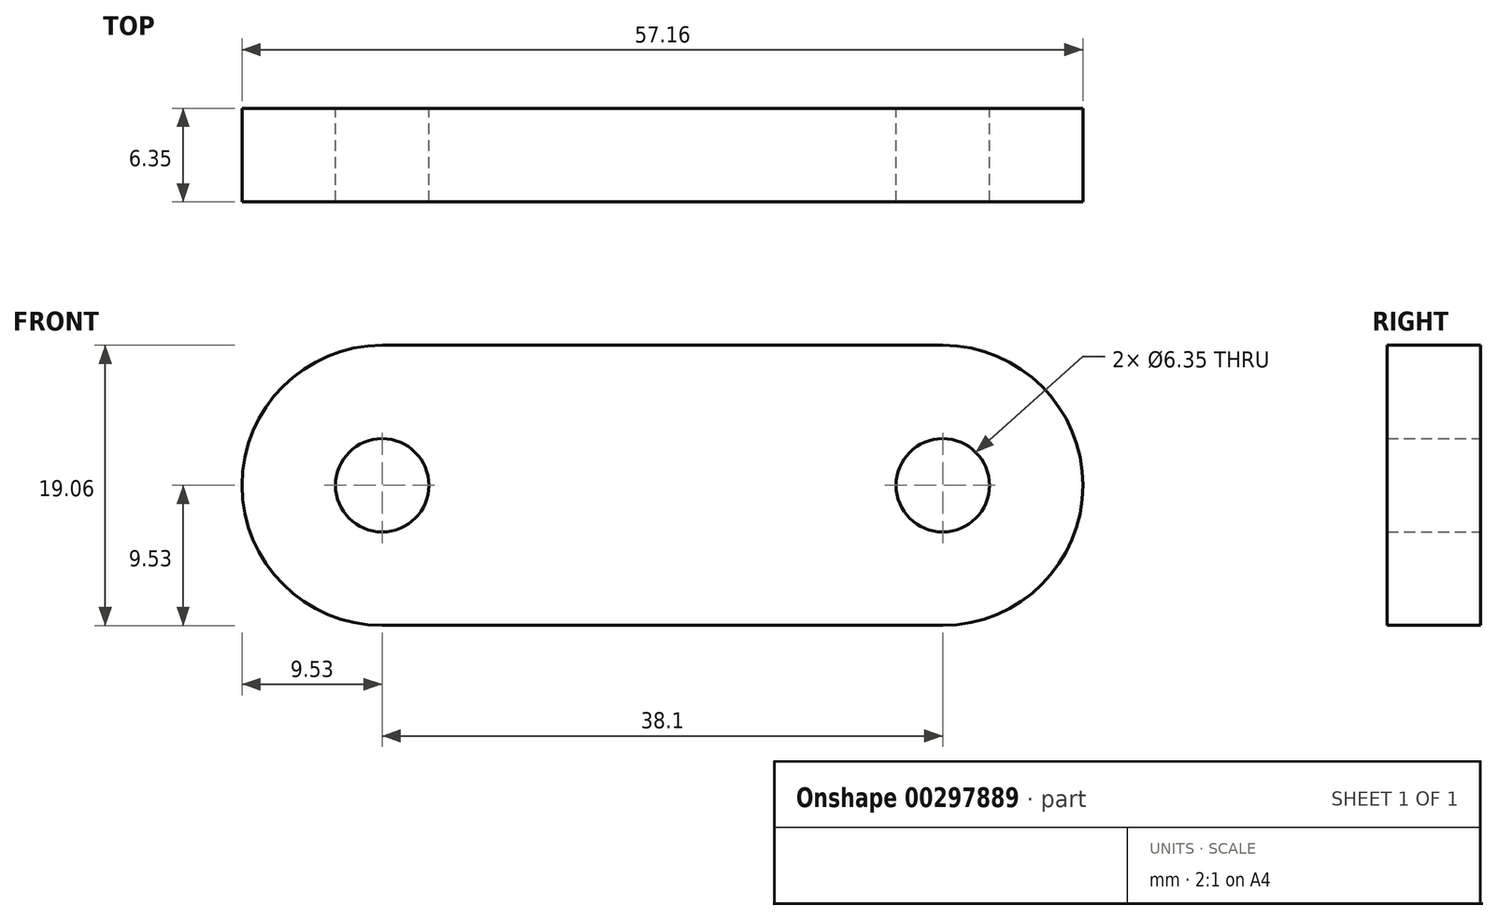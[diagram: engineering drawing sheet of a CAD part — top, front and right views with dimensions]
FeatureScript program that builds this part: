
annotation { "Feature Type Name" : "Feature", "Feature Type Description" : "" }
export const myFeature = defineFeature(function(context is Context, id is Id, definition is map)
    precondition{}
    {
        {
            var Q0;
            Q0=qCreatedBy(makeId("Front.planeOp"),FACE);
            var sketch = newSketch(context, id + "F0", { "sketchPlane" : qUnion([Q0])});
            skLineSegment(sketch, "E0.bottom", {"start": v(-19.05, 9.53) * mm, "end": v(19.05, 9.53) * mm});
            skLineSegment(sketch, "E0.top", {"start": v(-19.05, -9.53) * mm, "end": v(19.05, -9.53) * mm});
            skLineSegment(sketch, "E0.left", {"start": v(-19.05, 9.53) * mm, "end": v(-19.05, -9.53) * mm});
            skLineSegment(sketch, "E0.right", {"start": v(19.05, 9.53) * mm, "end": v(19.05, -9.53) * mm});
            skPoint(sketch, "E0.middle", {"position": v(0, 0) * mm});
            skArc(sketch, "E1", {"start": v(-19.05, 9.53) * mm, "mid": v(-28.58, 0) * mm, "end": v(-19.05, -9.53) * mm});
            skArc(sketch, "E2", {"start": v(19.05, -9.53) * mm, "mid": v(28.58, 0) * mm, "end": v(19.05, 9.53) * mm});
            skCircle(sketch, "E3", {"center": v(-19.05, 0) * mm, "radius": 3.18 * mm});
            skCircle(sketch, "E4", {"center": v(19.05, 0) * mm, "radius": 3.18 * mm});
            skSolve(sketch);
        }
        {
            var Q0;
            {var subQ5=sQuery(id+"F0.wireOp",EDGE,"E0.bottom");Q0=makeQuery(id+"F0.imprint","IMPRINT",FACE,{"disambiguationData":[TD([[makeQuery(id+"F0.imprint","IMPRINT",EDGE,{"derivedFrom":subQ5}),-1.0]])]});}
            var Q1;
            {var subQ0=sQuery(id+"F0.wireOp",EDGE,"E1");Q1=makeQuery(id+"F0.imprint","IMPRINT",FACE,{"disambiguationData":[TD([[makeQuery(id+"F0.imprint","IMPRINT",EDGE,{"derivedFrom":subQ0}),1.0]])]});}
            var Q2;
            {var subQ0=sQuery(id+"F0.wireOp",EDGE,"E2");Q2=makeQuery(id+"F0.imprint","IMPRINT",FACE,{"disambiguationData":[TD([[makeQuery(id+"F0.imprint","IMPRINT",EDGE,{"derivedFrom":subQ0}),1.0]])]});}
            extrude(context, id + "F1", {"entities" : qUnion([Q0, Q1, Q2]), "depth" : 6.35 * mm});
        }
    });
